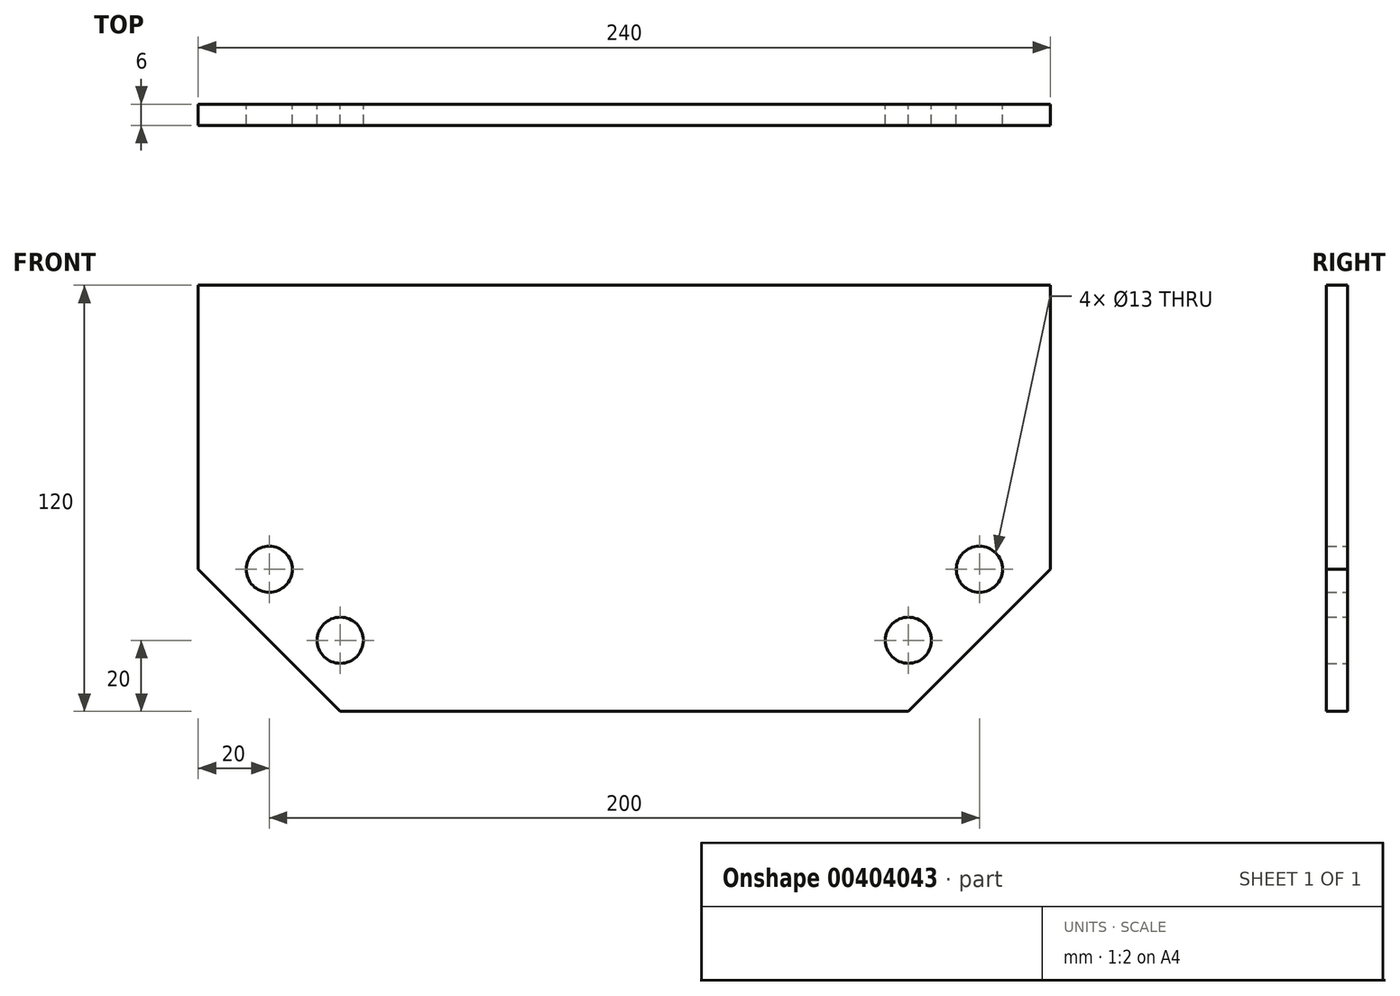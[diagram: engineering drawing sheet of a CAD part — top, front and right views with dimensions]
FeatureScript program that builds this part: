
annotation { "Feature Type Name" : "Feature", "Feature Type Description" : "" }
export const myFeature = defineFeature(function(context is Context, id is Id, definition is map)
    precondition{}
    {
        {
            var Q0;
            Q0=qCreatedBy(makeId("Front.planeOp"),FACE);
            var sketch = newSketch(context, id + "F0", { "sketchPlane" : qUnion([Q0])});
            skLineSegment(sketch, "E0", {"start": v(-120, 0) * mm, "end": v(-120, -80) * mm});
            skLineSegment(sketch, "E1", {"start": v(-120, -80) * mm, "end": v(-80, -120) * mm});
            skCircle(sketch, "E2", {"center": v(-80, -100) * mm, "radius": 6.5 * mm});
            skCircle(sketch, "E3", {"center": v(-100, -80) * mm, "radius": 6.5 * mm});
            skPoint(sketch, "E4.end.orphan", {"position": v(0, -120) * mm});
            skLineSegment(sketch, "E5", {"start": v(-120, 0) * mm, "end": v(120, 0) * mm});
            skLineSegment(sketch, "E6", {"start": v(120, 0) * mm, "end": v(120, -80) * mm});
            skLineSegment(sketch, "E7", {"start": v(120, -80) * mm, "end": v(80, -120) * mm});
            skLineSegment(sketch, "E8", {"start": v(80, -120) * mm, "end": v(-80, -120) * mm});
            skCircle(sketch, "E9", {"center": v(100, -80) * mm, "radius": 6.5 * mm});
            skCircle(sketch, "E10", {"center": v(80, -100) * mm, "radius": 6.5 * mm});
            skSolve(sketch);
        }
        {
            var Q0;
            Q0=makeQuery(id+"F0.imprint","IMPRINT",FACE,{"disambiguationData":[TD([[makeQuery(id+"F0.imprint","IMPRINT",EDGE,{"derivedFrom":sQuery(id+"F0.wireOp",EDGE,"E0")}),1.0]])]});
            extrude(context, id + "F1", {"entities" : qUnion([Q0]), "depth" : 6 * mm});
        }
    });
